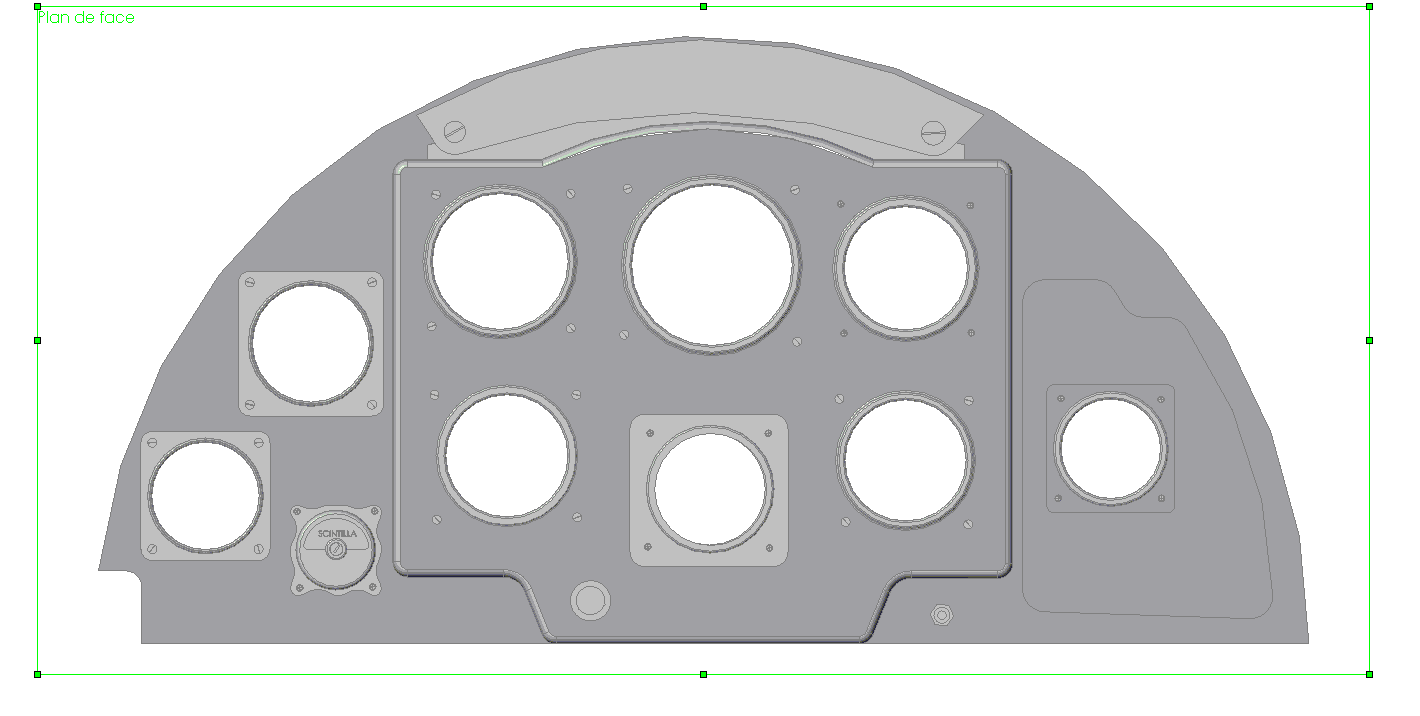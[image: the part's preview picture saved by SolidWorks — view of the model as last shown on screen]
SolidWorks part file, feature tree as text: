
SOLIDWORKS PART (.sldprt)
format: sldprt  version: not decoded by parser v0  size: 6,542,848 bytes
history: native  units: mm
features: sketch x158, cut_extrude x102, fillet x76, extrude x46, plane x4, mirror x2, material x1 (+8 scaffold rows collapsed)
feature tree (397):
  scaffold x8  (default folders/planes/origin — collapsed)
  material  "Matériau <non spécifié>"
  plane  "Plan de face"
  plane  "Plan de dessus"
  plane  "Plan de droite"
  sketch  "Esquisse1"  dims[c1.D1=80.0mm c1.D4=80.0mm c1.D2=168.0mm c1.D3=~80.158811mm c2.D1=80.4mm c2.D2=80.0mm c2.D3=80.4mm]
  extrude  "Extrusion1"  Depth=0.8mm
  sketch  "Esquisse2"
  extrude  "Extrusion2"  Depth=5mm
  fillet  "Congé1"  Radius=2mm
  fillet  "Congé2"  Radius=2mm
  sketch  "Esquisse3"  dims[D1=5.0mm D5=10.0mm D6=10.0mm D7=5.0mm]
  sketch  "Esquisse4"
  cut_extrude  "Enlèv. mat.-Extru.1"  Depth=5mm
  sketch  "Esquisse5"  dims[D1=~16.696445mm]
  cut_extrude  "Enlèv. mat.-Extru.2"  Depth=5mm
  fillet  "Congé3"  Radius=2mm
  fillet  "Congé4"  Radius=3mm
  fillet  "Congé5"  Radius=2mm
  fillet  "Congé6"  Radius=1mm
  sketch  "Esquisse6"
  extrude  "Extrusion3"  Depth=4mm
  sketch  "Esquisse7"  dims[D1=7.0mm]
  extrude  "Extrusion4"  Depth=5.5mm
  fillet  "Congé7"  Radius=3mm
  fillet  "Congé8"  Radius=3mm
  sketch  "Esquisse8"
  extrude  "Extrusion5"  Depth=0.3mm
  mirror  "Symétrie1"
  sketch  "Esquisse9"  dims[D1=~2.841949mm]
  extrude  "Extrusion6"  Depth=0.3mm
  sketch  "Esquisse13"
  cut_extrude  "Enlèv. mat.-Extru.14"  Depth=0.2mm
  sketch  "Esquisse14"
  cut_extrude  "Enlèv. mat.-Extru.15"  Depth=0.2mm
  sketch  "Esquisse15"
  extrude  "Extrusion7"  Depth=0.4mm
  sketch  "Esquisse20"
  extrude  "Extrusion8"  Depth=0.5mm
  sketch  "Esquisse22"
  cut_extrude  "Enlèv. mat.-Extru.16"  [1 undecoded]
  fillet  "Congé9"  Radius=1.5mm
  fillet  "Congé10"  Radius=1.5mm
  fillet  "Congé11"  Radius=1.5mm
  fillet  "Congé12"  Radius=1.5mm
  sketch  "Esquisse23"
  cut_extrude  "Enlèv. mat.-Extru.17"  Depth=0.2mm
  sketch  "Esquisse24"  dims[D1=1.2mm]
  cut_extrude  "Enlèv. mat.-Extru.18"  Depth=0.2mm
  sketch  "Esquisse25"
  cut_extrude  "Enlèv. mat.-Extru.19"  Depth=0.2mm
  sketch  "Esquisse26"
  cut_extrude  "Enlèv. mat.-Extru.20"  Depth=0.2mm
  sketch  "Esquisse27"  dims[D1=1.2mm]
  cut_extrude  "Enlèv. mat.-Extru.21"  Depth=0.2mm
  sketch  "Esquisse28"
  cut_extrude  "Enlèv. mat.-Extru.22"  Depth=0.2mm
  sketch  "Esquisse29"
  cut_extrude  "Enlèv. mat.-Extru.23"  Depth=0.2mm
  sketch  "Esquisse30"
  cut_extrude  "Enlèv. mat.-Extru.24"  Depth=0.2mm
  sketch  "Esquisse31"
  cut_extrude  "Enlèv. mat.-Extru.25"  [1 undecoded]
  sketch  "Esquisse32"
  cut_extrude  "Enlèv. mat.-Extru.26"  [1 undecoded]
  sketch  "Esquisse33"
  extrude  "Extrusion9"  Depth=0.4mm
  fillet  "Congé13"  Radius=1.5mm
  fillet  "Congé14"  Radius=1.5mm
  fillet  "Congé15"  Radius=1.5mm
  fillet  "Congé16"  Radius=1.5mm
  sketch  "Esquisse35"
  extrude  "Extrusion10"  Depth=0.5mm
  sketch  "Esquisse36"
  cut_extrude  "Enlèv. mat.-Extru.27"  [1 undecoded]
  sketch  "Esquisse37"
  cut_extrude  "Enlèv. mat.-Extru.28"  Depth=0.2mm
  sketch  "Esquisse38"
  cut_extrude  "Enlèv. mat.-Extru.29"  Depth=0.2mm
  sketch  "Esquisse39"
  cut_extrude  "Enlèv. mat.-Extru.30"  Depth=0.2mm
  sketch  "Esquisse40"
  cut_extrude  "Enlèv. mat.-Extru.31"  Depth=0.2mm
  fillet  "Congé17"  Radius=0.25mm
  fillet  "Congé18"  Radius=0.25mm
  fillet  "Congé19"  Radius=0.25mm
  fillet  "Congé20"  Radius=0.25mm
  sketch  "Esquisse41"
  cut_extrude  "Enlèv. mat.-Extru.32"  Depth=0.2mm
  sketch  "Esquisse42"
  cut_extrude  "Enlèv. mat.-Extru.33"  Depth=0.2mm
  sketch  "Esquisse43"
  cut_extrude  "Enlèv. mat.-Extru.34"  Depth=0.2mm
  sketch  "Esquisse44"
  cut_extrude  "Enlèv. mat.-Extru.35"  Depth=0.2mm
  sketch  "Esquisse48"
  extrude  "Extrusion12"  Depth=0.2mm
  sketch  "Esquisse49"
  cut_extrude  "Enlèv. mat.-Extru.38"  Depth=0.2mm
  sketch  "Esquisse50"
  cut_extrude  "Enlèv. mat.-Extru.39"  Depth=0.2mm
  sketch  "Esquisse51"
  cut_extrude  "Enlèv. mat.-Extru.40"  Depth=0.2mm
  sketch  "Esquisse52"
  cut_extrude  "Enlèv. mat.-Extru.41"  Depth=0.2mm
  mirror  "Symétrie11"
  plane  "Plan3"
  sketch  "Esquisse56"
  cut_extrude  "Enlèv. mat.-Extru.44"  Depth=0.2mm
  fillet  "Congé25"  Radius=1mm
  fillet  "Congé26"  Radius=1mm
  fillet  "Congé27"  Radius=1mm
  fillet  "Congé28"  Radius=1mm
  fillet  "Congé29"  Radius=1mm
  fillet  "Congé35"  Radius=2mm
  fillet  "Congé37"  Radius=2mm
  fillet  "Congé40"  Radius=2mm
  fillet  "Congé41"  Radius=2mm
  fillet  "Congé42"  Radius=2mm
  sketch  "Esquisse58"
  cut_extrude  "Enlèv. mat.-Extru.46"  Depth=0.2mm
  fillet  "Congé47"  Radius=3mm
  fillet  "Congé48"  Radius=3mm
  fillet  "Congé49"  Radius=3mm
  fillet  "Congé50"  Radius=3mm
  sketch  "Esquisse59"
  cut_extrude  "Enlèv. mat.-Extru.47"  Depth=0.2mm
  fillet  "Congé51"  Radius=3mm
  fillet  "Congé52"  Radius=3mm
  sketch  "Esquisse60"
  cut_extrude  "Enlèv. mat.-Extru.48"  Depth=0.2mm
  fillet  "Congé53"  Radius=3mm
  fillet  "Congé54"  Radius=3mm
  sketch  "Esquisse61"
  extrude  "Extrusion13"  Depth=1mm
  fillet  "Congé55"  Radius=0.5mm
  sketch  "Esquisse62"
  cut_extrude  "Enlèv. mat.-Extru.49"  Depth=0.3mm
  fillet  "Congé56"  Radius=0.5mm
  fillet  "Congé57"  Radius=0.5mm
  sketch  "Esquisse63"
  sketch  "Esquisse64"
  extrude  "Extrusion15"  Depth=0.5mm
  fillet  "Congé59"  Radius=0.2mm
  sketch  "Esquisse65"
  extrude  "Extrusion16"  Depth=0.1mm
  fillet  "Congé60"  Radius=0.05mm
  sketch  "Esquisse66"
  cut_extrude  "Enlèv. mat.-Extru.50"  Depth=0.5mm
  sketch  "Esquisse67"
  cut_extrude  "Enlèv. mat.-Extru.51"  Depth=0.1mm
  sketch  "Esquisse68"  dims[D1=~0.894999mm]
  extrude  "Extrusion18"  Depth=0.2mm
  fillet  "Congé61"  Radius=0.1mm
  sketch  "Esquisse69"
  cut_extrude  "Enlèv. mat.-Extru.52"  Depth=0.2mm
  sketch  "Esquisse70"
  extrude  "Extrusion19"  Depth=0.8mm
  sketch  "Esquisse71"
  extrude  "Extrusion20"  Depth=0.2mm
  sketch  "Esquisse72"
  extrude  "Extrusion21"  Depth=6mm
  sketch  "Esquisse76"  dims[D1=20.0mm]
  extrude  "Extrusion22"  Depth=0.5mm
  sketch  "Esquisse77"
  cut_extrude  "Enlèv. mat.-Extru.53"  [1 undecoded]
  fillet  "Congé62"  Radius=0.25mm
  fillet  "Congé63"  Radius=0.25mm
  sketch  "Esquisse78"
  extrude  "Extrusion23"  Depth=1mm
  sketch  "Esquisse79"
  extrude  "Extrusion24"  Depth=1mm
  sketch  "Esquisse80"
  extrude  "Extrusion25"  Depth=1mm
  sketch  "Esquisse81"
  extrude  "Extrusion26"  Depth=1mm
  sketch  "Esquisse82"
  extrude  "Extrusion27"  Depth=1mm
  sketch  "Esquisse83"
  extrude  "Extrusion28"  Depth=1mm
  sketch  "Esquisse84"
  cut_extrude  "Enlèv. mat.-Extru.54"  [1 undecoded]
  sketch  "Esquisse85"
  sketch  "Esquisse86"
  cut_extrude  "Enlèv. mat.-Extru.55"  [1 undecoded]
  sketch  "Esquisse87"
  cut_extrude  "Enlèv. mat.-Extru.56"  [1 undecoded]
  sketch  "Esquisse88"
  cut_extrude  "Enlèv. mat.-Extru.57"  [1 undecoded]
  sketch  "Esquisse89"
  cut_extrude  "Enlèv. mat.-Extru.58"  [1 undecoded]
  fillet  "Congé64"  Radius=0.25mm
  fillet  "Congé65"  Radius=0.25mm
  sketch  "Esquisse90"
  sketch  "Esquisse92"
  extrude  "Extrusion30"  Depth=1mm
  fillet  "Congé66"  Radius=3mm
  fillet  "Congé67"  Radius=3mm
  fillet  "Congé68"  Radius=3mm
  fillet  "Congé69"  Radius=3mm
  fillet  "Congé70"  Radius=3mm
  fillet  "Congé71"  Radius=3mm
  sketch  "Esquisse93"
  extrude  "Extrusion31"  Depth=0.8mm
  fillet  "Congé72"  Radius=1mm
  fillet  "Congé73"  Radius=1mm
  fillet  "Congé74"  Radius=1mm
  fillet  "Congé75"  Radius=1mm
  sketch  "Esquisse94"
  extrude  "Extrusion32"  Depth=2mm
  sketch  "Esquisse95"
  cut_extrude  "Enlèv. mat.-Extru.60"  [1 undecoded]
  fillet  "Congé76"  Radius=0.25mm
  sketch  "Esquisse96"
  extrude  "Extrusion33"  Depth=0.5mm
  sketch  "Esquisse97"
  extrude  "Extrusion34"  Depth=3mm
  sketch  "Esquisse98"
  cut_extrude  "Enlèv. mat.-Extru.61"  Depth=3mm
  sketch  "Esquisse100"
  cut_extrude  "Enlèv. mat.-Extru.62"  Depth=3mm
  sketch  "Esquisse101"
  sketch  "Esquisse102"
  cut_extrude  "Enlèv. mat.-Extru.63"  Depth=3mm
  sketch  "Esquisse103"
  cut_extrude  "Enlèv. mat.-Extru.64"  Depth=3mm
  sketch  "Esquisse104"  dims[D1=~0.894999mm]
  extrude  "Extrusion35"  Depth=0.2mm
  fillet  "Congé78"  Radius=0.1mm
  sketch  "Esquisse106"
  cut_extrude  "Enlèv. mat.-Extru.66"  Depth=0.2mm
  sketch  "Esquisse107"
  cut_extrude  "Enlèv. mat.-Extru.67"  Depth=0.2mm
  sketch  "Esquisse108"
  cut_extrude  "Enlèv. mat.-Extru.68"  Depth=0.2mm
  sketch  "1"  dims[D1=1.2mm]
  sketch  "3"  dims[D1=1.2mm]
  cut_extrude  "Enlèv. mat.-Extru.71"  Depth=0.2mm
  sketch  "4"
  cut_extrude  "Enlèv. mat.-Extru.72"  Depth=0.2mm
  sketch  "5"
  cut_extrude  "Enlèv. mat.-Extru.73"  Depth=0.2mm
  sketch  "6"
  cut_extrude  "Enlèv. mat.-Extru.74"  Depth=0.2mm
  sketch  "7"
  cut_extrude  "Enlèv. mat.-Extru.75"  Depth=0.2mm
  sketch  "8"
  cut_extrude  "Enlèv. mat.-Extru.76"  Depth=0.2mm
  sketch  "9"
  cut_extrude  "Enlèv. mat.-Extru.77"  Depth=0.2mm
  sketch  "10"
  cut_extrude  "Enlèv. mat.-Extru.78"  Depth=0.2mm
  sketch  "11"
  cut_extrude  "Enlèv. mat.-Extru.79"  Depth=0.2mm
  sketch  "12"
  cut_extrude  "Enlèv. mat.-Extru.80"  Depth=0.2mm
  sketch  "13"  dims[D1=1.2mm]
  cut_extrude  "Enlèv. mat.-Extru.81"  Depth=0.2mm
  sketch  "14"
  cut_extrude  "Enlèv. mat.-Extru.82"  Depth=0.2mm
  sketch  "Esquisse117"
  cut_extrude  "Enlèv. mat.-Extru.83"  Depth=4.2mm
  sketch  "Esquisse118"
  sketch  "Esquisse119"
  sketch  "Esquisse120"
  cut_extrude  "Enlèv. mat.-Extru.86"  Depth=4.2mm
  sketch  "Esquisse121"
  cut_extrude  "Enlèv. mat.-Extru.87"  Depth=4.2mm
  sketch  "Esquisse122"  dims[D1=14.0mm]
  sketch  "15"  dims[D1=1.2mm]
  cut_extrude  "Enlèv. mat.-Extru.88"  Depth=0.2mm
  sketch  "16"
  cut_extrude  "Enlèv. mat.-Extru.89"  Depth=0.2mm
  sketch  "19"  dims[D1=~0.894999mm]
  extrude  "Extrusion37"  Depth=0.2mm
  sketch  "Esquisse135"
  fillet  "Congé80"  Radius=0.1mm
  sketch  "20"
  cut_extrude  "Enlèv. mat.-Extru.91"  Depth=0.2mm
  sketch  "21"  dims[D1=~0.894999mm]
  extrude  "Extrusion38"  Depth=0.2mm
  fillet  "Congé81"  Radius=0.1mm
  sketch  "22"
  cut_extrude  "Enlèv. mat.-Extru.92"  Depth=0.2mm
  sketch  "23"  dims[D1=~0.894999mm]
  extrude  "Extrusion39"  Depth=0.2mm
  fillet  "Congé82"  Radius=0.1mm
  sketch  "24"
  cut_extrude  "Enlèv. mat.-Extru.93"  Depth=0.2mm
  sketch  "25"  dims[D1=~0.894999mm]
  extrude  "Extrusion40"  Depth=0.2mm
  fillet  "Congé83"  Radius=0.1mm
  sketch  "26"
  cut_extrude  "Enlèv. mat.-Extru.94"  Depth=0.2mm
  sketch  "27"  dims[D1=~0.894999mm]
  extrude  "Extrusion41"  Depth=0.2mm
  fillet  "Congé84"  Radius=0.1mm
  sketch  "28"
  cut_extrude  "Enlèv. mat.-Extru.95"  Depth=0.2mm
  sketch  "29"  dims[D1=~0.894999mm]
  extrude  "Extrusion42"  Depth=0.2mm
  fillet  "Congé85"  Radius=0.1mm
  sketch  "30"
  cut_extrude  "Enlèv. mat.-Extru.96"  Depth=0.2mm
  sketch  "31"  dims[D1=1.2mm]
  cut_extrude  "Enlèv. mat.-Extru.97"  Depth=0.2mm
  sketch  "32"
  cut_extrude  "Enlèv. mat.-Extru.98"  Depth=0.2mm
  sketch  "33"
  cut_extrude  "Enlèv. mat.-Extru.99"  Depth=0.2mm
  sketch  "34"
  cut_extrude  "Enlèv. mat.-Extru.100"  Depth=0.2mm
  sketch  "35"
  cut_extrude  "Enlèv. mat.-Extru.101"  Depth=0.2mm
  sketch  "36"
  cut_extrude  "Enlèv. mat.-Extru.102"  Depth=0.2mm
  sketch  "37"
  cut_extrude  "Enlèv. mat.-Extru.103"  Depth=0.2mm
  sketch  "38"
  cut_extrude  "Enlèv. mat.-Extru.104"  Depth=0.2mm
  sketch  "Esquisse161"
  extrude  "Extrusion43"  Depth=0.5mm
  sketch  "Esquisse162"
  cut_extrude  "Enlèv. mat.-Extru.105"  [1 undecoded]
  fillet  "Congé86"  Radius=2mm
  fillet  "Congé87"  Radius=2mm
  sketch  "39"  dims[D1=~0.894999mm]
  extrude  "Extrusion44"  Depth=0.2mm
  fillet  "Congé88"  Radius=0.1mm
  sketch  "40"
  cut_extrude  "Enlèv. mat.-Extru.106"  Depth=0.2mm
  sketch  "41"  dims[D1=~0.894999mm]
  extrude  "Extrusion45"  Depth=0.2mm
  fillet  "Congé89"  Radius=0.1mm
  sketch  "42"
  cut_extrude  "Enlèv. mat.-Extru.107"  Depth=0.2mm
  sketch  "43"  dims[D1=~0.894999mm]
  extrude  "Extrusion46"  Depth=0.2mm
  fillet  "Congé90"  Radius=0.1mm
  sketch  "44"
  cut_extrude  "Enlèv. mat.-Extru.108"  Depth=0.2mm
  sketch  "45"  dims[D1=~0.894999mm]
  extrude  "Extrusion47"  Depth=0.2mm
  fillet  "Congé91"  Radius=0.1mm
  sketch  "46"
  cut_extrude  "Enlèv. mat.-Extru.109"  Depth=0.2mm
  sketch  "47"
  cut_extrude  "Enlèv. mat.-Extru.110"  Depth=0.2mm
  sketch  "48"
  cut_extrude  "Enlèv. mat.-Extru.111"  Depth=0.2mm
  sketch  "49"
  cut_extrude  "Enlèv. mat.-Extru.112"  Depth=0.2mm
  sketch  "50"
  cut_extrude  "Enlèv. mat.-Extru.113"  Depth=0.2mm
  sketch  "51"
  cut_extrude  "Enlèv. mat.-Extru.114"  Depth=0.2mm
  sketch  "52"
  cut_extrude  "Enlèv. mat.-Extru.115"  Depth=0.2mm
  sketch  "53"
  cut_extrude  "Enlèv. mat.-Extru.116"  Depth=0.2mm
  sketch  "54"
  cut_extrude  "Enlèv. mat.-Extru.117"  Depth=0.2mm
  sketch  "55"  dims[D1=~0.894999mm]
  extrude  "Extrusion48"  Depth=0.2mm
  fillet  "Congé92"  Radius=0.1mm
  sketch  "56"
  cut_extrude  "Enlèv. mat.-Extru.118"  Depth=0.2mm
  sketch  "57"  dims[D1=~0.894999mm]
  extrude  "Extrusion49"  Depth=0.2mm
  fillet  "Congé93"  Radius=0.1mm
  sketch  "58"
  cut_extrude  "Enlèv. mat.-Extru.119"  Depth=0.2mm
  sketch  "59"  dims[D1=~0.894999mm]
  extrude  "Extrusion50"  Depth=0.2mm
  fillet  "Congé94"  Radius=0.1mm
  sketch  "60"
  cut_extrude  "Enlèv. mat.-Extru.120"  Depth=0.2mm
  sketch  "61"  dims[D1=~0.894999mm]
  extrude  "Extrusion51"  Depth=0.2mm
  fillet  "Congé95"  Radius=0.1mm
  sketch  "62"
  cut_extrude  "Enlèv. mat.-Extru.121"  Depth=0.2mm
  sketch  "Esquisse187"
  cut_extrude  "Enlèv. mat.-Extru.122"  Depth=4mm
  sketch  "Esquisse188"
  cut_extrude  "Enlèv. mat.-Extru.123"  Depth=4mm
  sketch  "Esquisse189"
  cut_extrude  "Enlèv. mat.-Extru.124"  Depth=4mm
  sketch  "Esquisse190"  dims[D1=15.0mm]
  cut_extrude  "Enlèv. mat.-Extru.125"  Depth=2mm
decode coverage: 243 of 384 modeling features carry decoded parameters
note: ~ marks probable driven/reference dimensions
note: 12 parameter values undecoded
summary: no parameter record found for 12 features
note: suppression state not decoded; provenance and decode notes live in map.json
